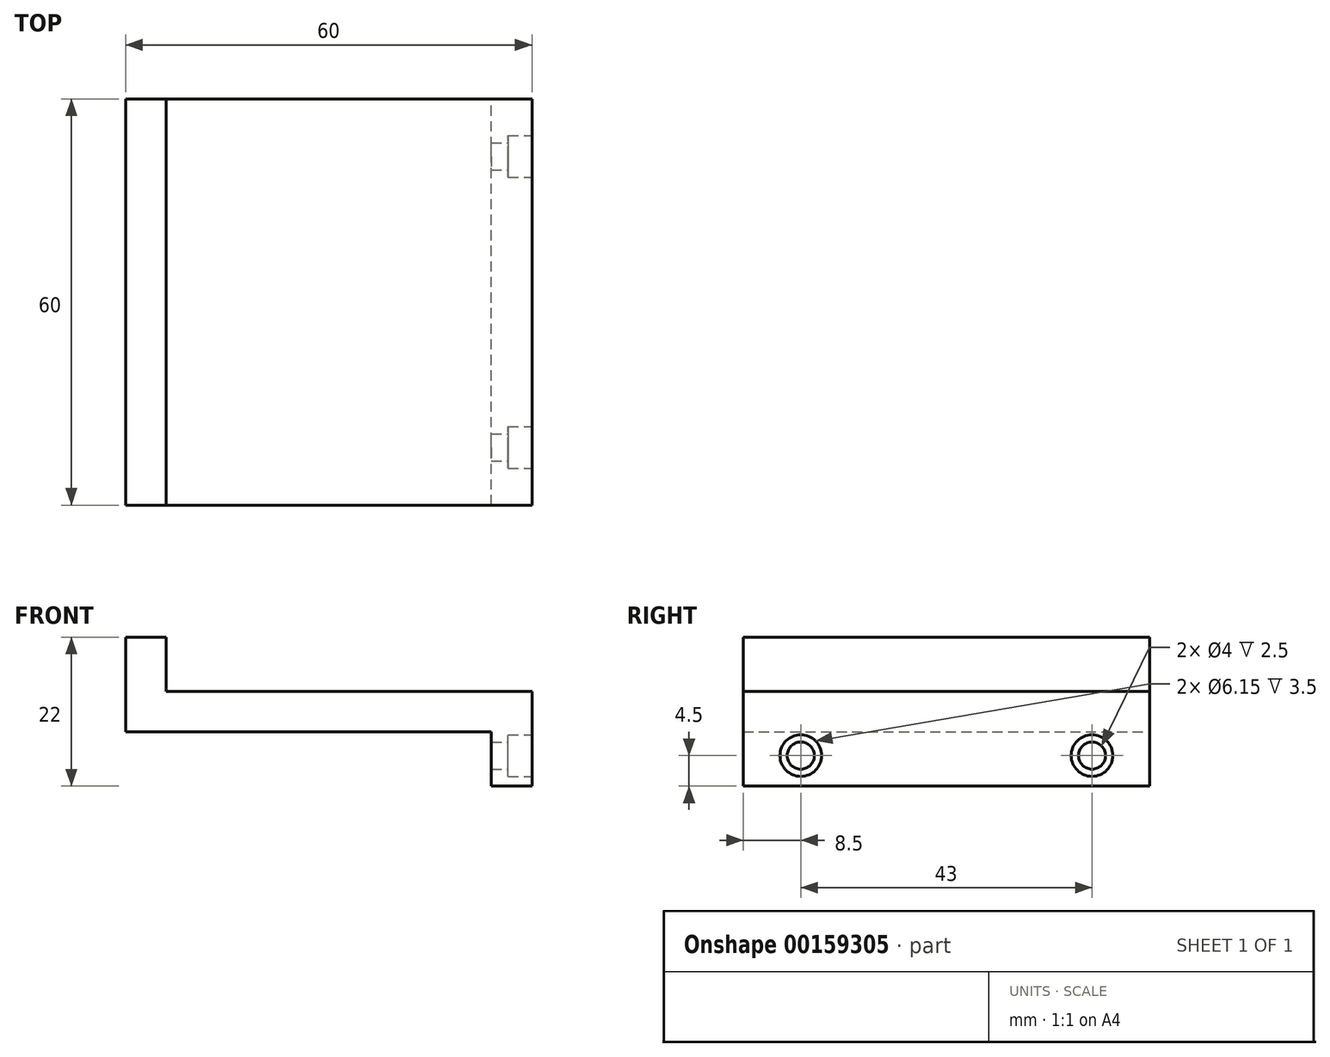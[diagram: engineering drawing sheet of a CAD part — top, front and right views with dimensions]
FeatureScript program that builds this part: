
annotation { "Feature Type Name" : "Feature", "Feature Type Description" : "" }
export const myFeature = defineFeature(function(context is Context, id is Id, definition is map)
    precondition{}
    {
        {
            var Q0;
            Q0=qCreatedBy(makeId("Top.planeOp"),FACE);
            var sketch = newSketch(context, id + "F0", { "sketchPlane" : qUnion([Q0])});
            skLineSegment(sketch, "E0.bottom", {"start": v(30, 30) * mm, "end": v(-30, 30) * mm});
            skLineSegment(sketch, "E0.top", {"start": v(30, -30) * mm, "end": v(-30, -30) * mm});
            skLineSegment(sketch, "E0.left", {"start": v(30, 30) * mm, "end": v(30, -30) * mm});
            skLineSegment(sketch, "E0.right", {"start": v(-30, 30) * mm, "end": v(-30, -30) * mm});
            skPoint(sketch, "E0.middle", {"position": v(0, 0) * mm});
            skSolve(sketch);
        }
        {
            var Q0;
            Q0 = qSketchRegion(id + "F0", true);
            extrude(context, id + "F1", {"entities" : qUnion([Q0]), "depth" : 22 * mm});
        }
        {
            var Q0;
            Q0=makeQuery(id+"F1.opExtrude","CAP_FACE",FACE,{"disambiguationData":[OSD([sQuery(id+"F0.wireOp",EDGE,"E0.bottom"),sQuery(id+"F0.wireOp",EDGE,"E0.top"),sQuery(id+"F0.wireOp",EDGE,"E0.left"),sQuery(id+"F0.wireOp",EDGE,"E0.right")])],"isStart":false});
            var sketch = newSketch(context, id + "F2", { "sketchPlane" : qUnion([Q0])});
            skLineSegment(sketch, "E1.bottom", {"start": v(-24, 36.62) * mm, "end": v(41.94, 36.62) * mm});
            skLineSegment(sketch, "E1.top", {"start": v(-24, -36.62) * mm, "end": v(41.94, -36.62) * mm});
            skLineSegment(sketch, "E1.left", {"start": v(-24, 36.62) * mm, "end": v(-24, -36.62) * mm});
            skLineSegment(sketch, "E1.right", {"start": v(41.94, 36.62) * mm, "end": v(41.94, -36.62) * mm});
            skPoint(sketch, "E1.middle", {"position": v(8.97, 0) * mm});
            skSolve(sketch);
        }
        {
            var Q0;
            Q0 = qSketchRegion(id + "F2", true);
            extrude(context, id + "F3", {"entities" : qUnion([Q0]), "operationType" : NewBodyOperationType.REMOVE, "oppositeDirection" : true, "depth" : 8 * mm});
        }
        {
            var Q0;
            Q0=makeQuery(id+"F1.opExtrude","CAP_FACE",FACE,{"disambiguationData":[OSD([sQuery(id+"F0.wireOp",EDGE,"E0.bottom"),sQuery(id+"F0.wireOp",EDGE,"E0.top"),sQuery(id+"F0.wireOp",EDGE,"E0.left"),sQuery(id+"F0.wireOp",EDGE,"E0.right")])],"isStart":true});
            var sketch = newSketch(context, id + "F4", { "sketchPlane" : qUnion([Q0])});
            skLineSegment(sketch, "E2.bottom", {"start": v(24, 34.98) * mm, "end": v(-42.14, 34.98) * mm});
            skLineSegment(sketch, "E2.top", {"start": v(24, -34.98) * mm, "end": v(-42.14, -34.98) * mm});
            skLineSegment(sketch, "E2.left", {"start": v(24, 34.98) * mm, "end": v(24, -34.98) * mm});
            skLineSegment(sketch, "E2.right", {"start": v(-42.14, 34.98) * mm, "end": v(-42.14, -34.98) * mm});
            skPoint(sketch, "E2.middle", {"position": v(-9.07, 0) * mm});
            skPoint(sketch, "E2.middle.positionSnap0", {"position": v(-30, 0) * mm});
            skPoint(sketch, "E2.centerSnap0", {"position": v(-30, 0) * mm});
            skSolve(sketch);
        }
        {
            var Q0;
            Q0 = qSketchRegion(id + "F4", true);
            extrude(context, id + "F5", {"entities" : qUnion([Q0]), "operationType" : NewBodyOperationType.REMOVE, "oppositeDirection" : true, "depth" : 8 * mm});
        }
        {
            var Q0;
            Q0=makeQuery(id+"F1.opExtrude","SWEPT_FACE",FACE,{"disambiguationData":[OSD([sQuery(id+"F0.wireOp",EDGE,"E0.left")])]});
            var sketch = newSketch(context, id + "F6", { "sketchPlane" : qUnion([Q0])});
            skCircle(sketch, "E3", {"center": v(21.5, 4.5) * mm, "radius": 2 * mm});
            skCircle(sketch, "E4.MirrorC", {"center": v(-21.5, 4.5) * mm, "radius": 2 * mm});
            skSolve(sketch);
        }
        {
            var Q0;
            Q0 = qSketchRegion(id + "F6", true);
            extrude(context, id + "F7", {"entities" : qUnion([Q0]), "operationType" : NewBodyOperationType.REMOVE, "oppositeDirection" : true, "depth" : 8 * mm});
        }
        {
            var Q0;
            Q0=makeQuery(id+"F1.opExtrude","SWEPT_FACE",FACE,{"disambiguationData":[OSD([sQuery(id+"F0.wireOp",EDGE,"E0.left")])]});
            var sketch = newSketch(context, id + "F8", { "sketchPlane" : qUnion([Q0])});
            skCircle(sketch, "E5", {"center": v(-21.5, 4.5) * mm, "radius": 3.07 * mm});
            skCircle(sketch, "E6.MirrorC", {"center": v(21.5, 4.5) * mm, "radius": 3.07 * mm});
            skSolve(sketch);
        }
        {
            var Q0;
            Q0 = qSketchRegion(id + "F8", true);
            extrude(context, id + "F9", {"entities" : qUnion([Q0]), "operationType" : NewBodyOperationType.REMOVE, "oppositeDirection" : true, "depth" : 3.5 * mm});
        }
    });
